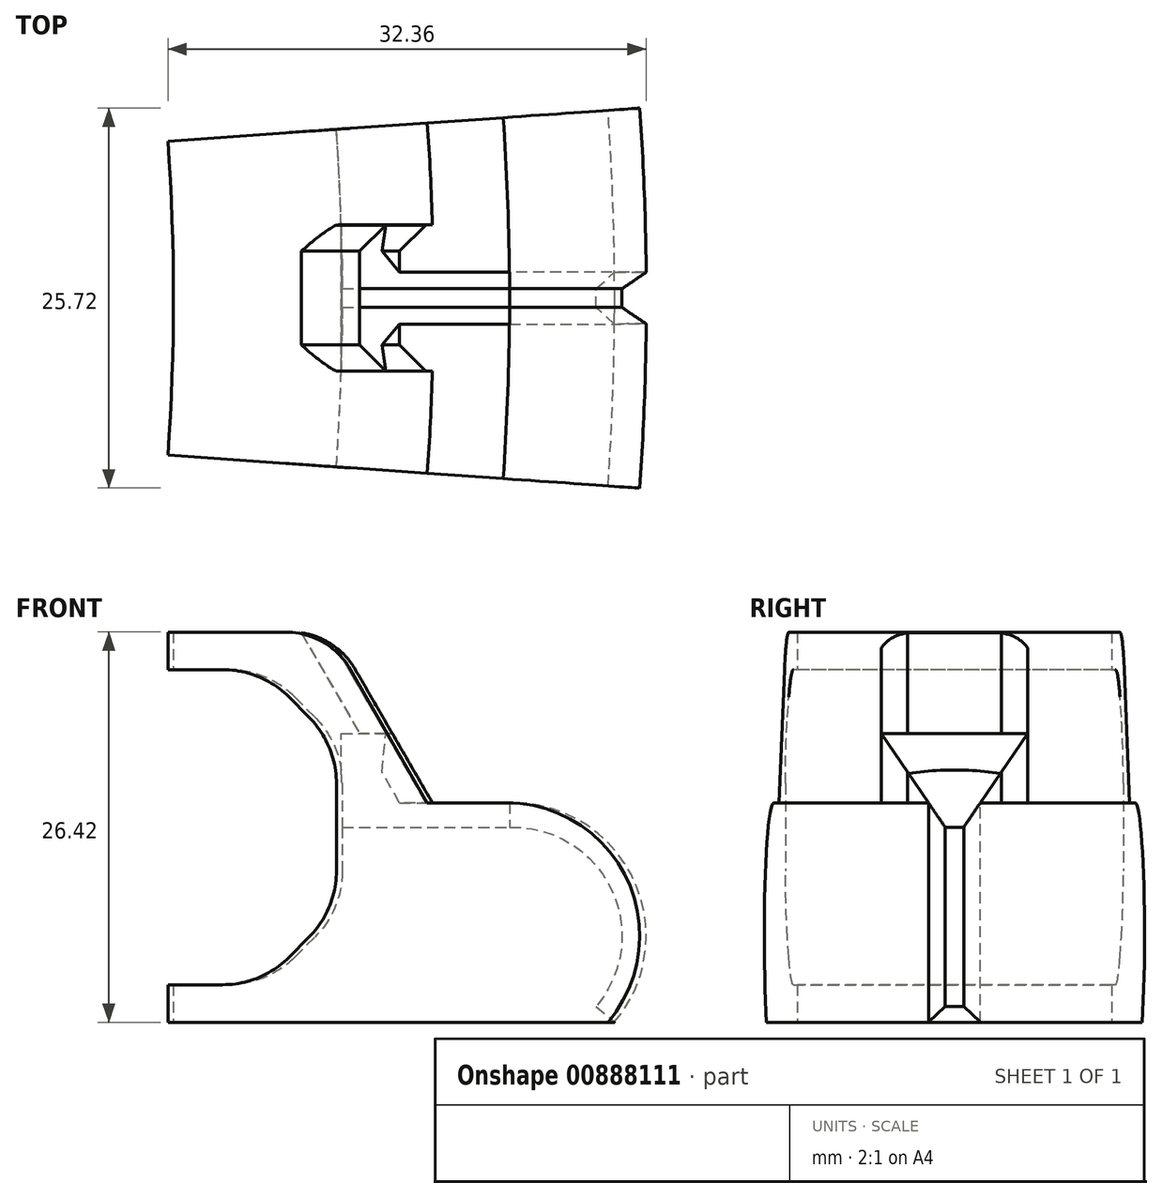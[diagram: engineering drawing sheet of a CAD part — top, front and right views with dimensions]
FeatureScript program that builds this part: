
annotation { "Feature Type Name" : "Feature", "Feature Type Description" : "" }
export const myFeature = defineFeature(function(context is Context, id is Id, definition is map)
    precondition{}
    {
        {
            var Q0;
            Q0=qCreatedBy(makeId("Front.planeOp"),FACE);
            var sketch = newSketch(context, id + "F0", { "sketchPlane" : qUnion([Q0])});
            skLineSegment(sketch, "E0", {"start": v(0, 0) * mm, "end": v(29.86, 0) * mm});
            skLineSegment(sketch, "E1", {"start": v(10.92, 26.42) * mm, "end": v(0, 26.42) * mm});
            skLineSegment(sketch, "E2", {"start": v(0, 26.42) * mm, "end": v(0, 23.88) * mm});
            skLineSegment(sketch, "E3", {"start": v(0, 23.88) * mm, "end": v(11.43, 23.88) * mm});
            skLineSegment(sketch, "E4", {"start": v(11.43, 23.88) * mm, "end": v(11.43, 2.54) * mm});
            skLineSegment(sketch, "E5", {"start": v(11.43, 2.54) * mm, "end": v(0, 2.54) * mm});
            skLineSegment(sketch, "E6", {"start": v(0, 2.54) * mm, "end": v(0, 0) * mm});
            skLineSegment(sketch, "E7", {"start": v(17.6, 14.86) * mm, "end": v(10.92, 26.42) * mm});
            skArc(sketch, "E8", {"start": v(29.86, 0) * mm, "mid": v(31.12, 9.74) * mm, "end": v(22.74, 14.86) * mm});
            skLineSegment(sketch, "E9", {"start": v(22.74, 14.86) * mm, "end": v(17.6, 14.86) * mm});
            skPoint(sketch, "E10.start.orphan", {"position": v(22.99, 0) * mm});
            skSolve(sketch);
        }
        {
            var Q0;
            Q0=qCreatedBy(makeId("Front.planeOp"),FACE);
            var sketch = newSketch(context, id + "F1", { "sketchPlane" : qUnion([Q0])});
            skLineSegment(sketch, "E11.1", {"start": v(17.6, 14.86) * mm, "end": v(10.92, 26.42) * mm});
            skSolve(sketch);
        }
        {
            var Q0;
            Q0=qCreatedBy(makeId("Top.planeOp"),FACE);
            var sketch = newSketch(context, id + "F2", { "sketchPlane" : qUnion([Q0])});
            skPoint(sketch, "E12", {"position": v(-120.8, 16.23) * mm});
            skArc(sketch, "E13", {"start": v(-0.37, -10.63) * mm, "mid": v(0, 0) * mm, "end": v(-0.37, 10.63) * mm});
            skLineSegment(sketch, "E14", {"start": v(-152.4, 0) * mm, "end": v(51.78, -14.28) * mm, "construction": true});
            skLineSegment(sketch, "E15", {"start": v(-152.4, 0) * mm, "end": v(9.98, 11.35) * mm, "construction": true});
            skSolve(sketch);
        }
        {
            var Q0;
            Q0=qCreatedBy(makeId("Right.planeOp"),FACE);
            cPlane(context, id + "F3", {"entities" : qUnion([Q0]), "cplaneType" : CPlaneType.OFFSET, "offset" : 16.5 * mm, "width" : 152.4 * mm, "height" : 152.4 * mm});
        }
        {
            var Q0;
            Q0=qCreatedBy(makeId("Front.planeOp"),FACE);
            var sketch = newSketch(context, id + "F4", { "sketchPlane" : qUnion([Q0])});
            skLineSegment(sketch, "E16.0", {"start": v(22.74, 14.86) * mm, "end": v(17.6, 14.86) * mm});
            skArc(sketch, "E16.1", {"start": v(29.86, 0) * mm, "mid": v(31.12, 9.74) * mm, "end": v(22.74, 14.86) * mm});
            skLineSegment(sketch, "E17", {"start": v(17.6, 14.86) * mm, "end": v(11.36, 14.86) * mm});
            skSolve(sketch);
        }
        {
            var Q0;
            Q0=qSketchRegion(id+"F0",true);
            var Q1;
            Q1=qConstructionFilter(qBodyType(qCreatedBy(id+"F2",EDGE),BodyType.WIRE),ConstructionObject.NO);
            sweep(context, id + "F5", {"profiles" : qUnion([Q0]), "path" : qUnion([Q1])});
        }
        {
            var Q0;
            Q0=qCreatedBy(id+"F3.planeOp",FACE);
            var sketch = newSketch(context, id + "F6", { "sketchPlane" : qUnion([Q0])});
            skLineSegment(sketch, "E18", {"start": v(4.95, 19.56) * mm, "end": v(-4.95, 19.56) * mm});
            skLineSegment(sketch, "E19", {"start": v(-4.95, 19.56) * mm, "end": v(-0.63, 13.2) * mm});
            skLineSegment(sketch, "E20", {"start": v(-0.64, 13.2) * mm, "end": v(0.64, 13.2) * mm});
            skLineSegment(sketch, "E21", {"start": v(0.64, 13.2) * mm, "end": v(4.95, 19.56) * mm});
            skSolve(sketch);
        }
        {
            var Q0;
            Q0=makeQuery(id+"F5.opSweep","SWEPT_EDGE",EDGE,{"disambiguationData":[OSD([sQuery(id+"F0.wireOp",EDGE,"E3"),sQuery(id+"F0.wireOp",EDGE,"E4"),sQuery(id+"F2.wireOp",EDGE,"XsQ3B0yG-sA46-cVKs-8mzo-xuo9gTvsWvxH")])]});
            var Q1;
            Q1=makeQuery(id+"F5.opSweep","SWEPT_EDGE",EDGE,{"disambiguationData":[OSD([sQuery(id+"F0.wireOp",EDGE,"E4"),sQuery(id+"F0.wireOp",EDGE,"E5"),sQuery(id+"F2.wireOp",EDGE,"XsQ3B0yG-sA46-cVKs-8mzo-xuo9gTvsWvxH")])]});
            chamfer(context, id + "F7", {"entities" : qUnion([Q0, Q1]), "width" : 5.08 * mm, "tangentPropagation" : true});
        }
        {
            var Q0;
            {var subQ0=sQuery(id+"F2.wireOp",EDGE,"XsQ3B0yG-sA46-cVKs-8mzo-xuo9gTvsWvxH");var subQ1=sQuery(id+"F0.wireOp",EDGE,"E4");Q0=makeQuery(id+"F7.opChamfer","BLEND_EDGE",EDGE,{"blendedFrom":[makeQuery(id+"F5.opSweep","SWEPT_EDGE",EDGE,{"disambiguationData":[OSD([subQ1,sQuery(id+"F0.wireOp",EDGE,"E5"),subQ0])]}),makeQuery(id+"F5.opSweep","SWEPT_FACE",FACE,{"disambiguationData":[OSD([subQ1,subQ0])]})],"blendedInto":[makeQuery(id+"F5.opSweep","SWEPT_FACE",FACE,{"disambiguationData":[OSD([subQ1,subQ0])]})]});}
            var Q1;
            {var subQ0=sQuery(id+"F2.wireOp",EDGE,"XsQ3B0yG-sA46-cVKs-8mzo-xuo9gTvsWvxH");var subQ1=sQuery(id+"F0.wireOp",EDGE,"E5");Q1=makeQuery(id+"F7.opChamfer","BLEND_EDGE",EDGE,{"blendedFrom":[makeQuery(id+"F5.opSweep","SWEPT_EDGE",EDGE,{"disambiguationData":[OSD([sQuery(id+"F0.wireOp",EDGE,"E4"),subQ1,subQ0])]}),makeQuery(id+"F5.opSweep","SWEPT_FACE",FACE,{"disambiguationData":[OSD([subQ1,subQ0])]})],"blendedInto":[makeQuery(id+"F5.opSweep","SWEPT_FACE",FACE,{"disambiguationData":[OSD([subQ1,subQ0])]})]});}
            var Q2;
            {var subQ0=sQuery(id+"F2.wireOp",EDGE,"XsQ3B0yG-sA46-cVKs-8mzo-xuo9gTvsWvxH");var subQ1=sQuery(id+"F0.wireOp",EDGE,"E3");Q2=makeQuery(id+"F7.opChamfer","BLEND_EDGE",EDGE,{"blendedFrom":[makeQuery(id+"F5.opSweep","SWEPT_EDGE",EDGE,{"disambiguationData":[OSD([subQ1,sQuery(id+"F0.wireOp",EDGE,"E4"),subQ0])]}),makeQuery(id+"F5.opSweep","SWEPT_FACE",FACE,{"disambiguationData":[OSD([subQ1,subQ0])]})],"blendedInto":[makeQuery(id+"F5.opSweep","SWEPT_FACE",FACE,{"disambiguationData":[OSD([subQ1,subQ0])]})]});}
            var Q3;
            {var subQ0=sQuery(id+"F2.wireOp",EDGE,"XsQ3B0yG-sA46-cVKs-8mzo-xuo9gTvsWvxH");var subQ1=sQuery(id+"F0.wireOp",EDGE,"E4");Q3=makeQuery(id+"F7.opChamfer","BLEND_EDGE",EDGE,{"blendedFrom":[makeQuery(id+"F5.opSweep","SWEPT_EDGE",EDGE,{"disambiguationData":[OSD([sQuery(id+"F0.wireOp",EDGE,"E3"),subQ1,subQ0])]}),makeQuery(id+"F5.opSweep","SWEPT_FACE",FACE,{"disambiguationData":[OSD([subQ1,subQ0])]})],"blendedInto":[makeQuery(id+"F5.opSweep","SWEPT_FACE",FACE,{"disambiguationData":[OSD([subQ1,subQ0])]})]});}
            fillet(context, id + "F8", {"entities" : qUnion([Q0, Q1, Q2, Q3]), "radius" : 6.35 * mm, "tangentPropagation" : true, "allowEdgeOverflow" : false});
        }
        {
            var Q0;
            Q0=qSketchRegion(id+"F6",true);
            var Q1;
            Q1=qConstructionFilter(qBodyType(qCreatedBy(id+"F6",EDGE),BodyType.WIRE),ConstructionObject.NO);
            var Q2;
            Q2=qConstructionFilter(qBodyType(qCreatedBy(id+"F4",EDGE),BodyType.WIRE),ConstructionObject.NO);
            sweep(context, id + "F9", {"operationType" : NewBodyOperationType.REMOVE, "profiles" : qUnion([Q0]), "surfaceProfiles" : qUnion([Q1]), "path" : qUnion([Q2])});
        }
        {
            var Q0;
            Q0=makeQuery(id+"F5.opSweep","SWEPT_FACE",FACE,{"disambiguationData":[OSD([sQuery(id+"F0.wireOp",EDGE,"E1"),sQuery(id+"F2.wireOp",EDGE,"E13")])]});
            var sketch = newSketch(context, id + "F10", { "sketchPlane" : qUnion([Q0])});
            skLineSegment(sketch, "E22", {"start": v(8.64, 0) * mm, "end": v(8.64, 3.18) * mm});
            skPoint(sketch, "E22.startSnap0", {"position": v(10.92, 0) * mm});
            skLineSegment(sketch, "E23", {"start": v(8.64, 3.18) * mm, "end": v(10.4, 4.95) * mm});
            skLineSegment(sketch, "E24.MirrorCS", {"start": v(8.64, -3.18) * mm, "end": v(10.4, -4.95) * mm});
            skLineSegment(sketch, "E25.MirrorCS", {"start": v(8.64, 0) * mm, "end": v(8.64, -3.18) * mm});
            skLineSegment(sketch, "E26", {"start": v(11.18, 4.99) * mm, "end": v(11.18, -4.95) * mm});
            skLineSegment(sketch, "E27", {"start": v(10.4, 4.95) * mm, "end": v(11.18, 4.99) * mm});
            skLineSegment(sketch, "E28", {"start": v(11.18, -4.95) * mm, "end": v(10.4, -4.95) * mm});
            skSolve(sketch);
        }
        {
            var Q0;
            Q0=qSketchRegion(id+"F10",true);
            var Q1;
            Q1=qConstructionFilter(qBodyType(qCreatedBy(id+"F1",EDGE),BodyType.WIRE),ConstructionObject.NO);
            sweep(context, id + "F11", {"operationType" : NewBodyOperationType.REMOVE, "profiles" : qUnion([Q0]), "path" : qUnion([Q1])});
        }
        {
            var Q0;
            Q0=makeQuery(id+"F5.opSweep","SWEPT_EDGE",EDGE,{"disambiguationData":[OSD([sQuery(id+"F0.wireOp",EDGE,"E1"),sQuery(id+"F0.wireOp",EDGE,"E7"),sQuery(id+"F2.wireOp",EDGE,"XsQ3B0yG-sA46-cVKs-8mzo-xuo9gTvsWvxH")])]});
            fillet(context, id + "F12", {"entities" : qUnion([Q0]), "radius" : 5.08 * mm, "tangentPropagation" : true, "allowEdgeOverflow" : false});
        }
    });
